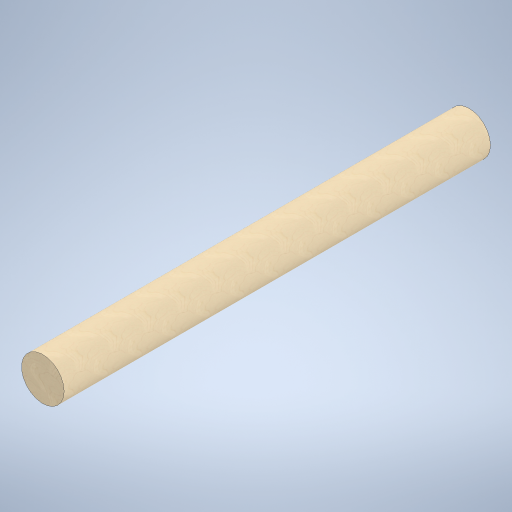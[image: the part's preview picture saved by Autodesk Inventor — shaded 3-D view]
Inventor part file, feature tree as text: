
AUTODESK INVENTOR PART (.ipt)
format: ipt  version: 2024 (Build 280153000, 153)  size: 288,256 bytes
history: native  units: in
note: dims shown in document units (in); Inventor stores cm internally (conversion verified against a paired STEP export)
features: extrude x1, direct_edit x1, sketch x1, other x1
ambient origin geometry x8: Origin, YZ Plane, XZ Plane, XY Plane, X Axis, Y Axis, Z Axis, Center Point
bodies: Solid1 (feature_tree)
feature tree (4):
  extrude  "Extrusion1"  Depth=0.3937in TaperAngle=0.0deg
  direct_edit  "Direct Edit1"
  sketch  "Sketch1"  dims[d0=0.125in d1=1.25in d2=0.0in d3=3.937in d4=0.3937in d5=0.3937in]
  other  "Scale1"
